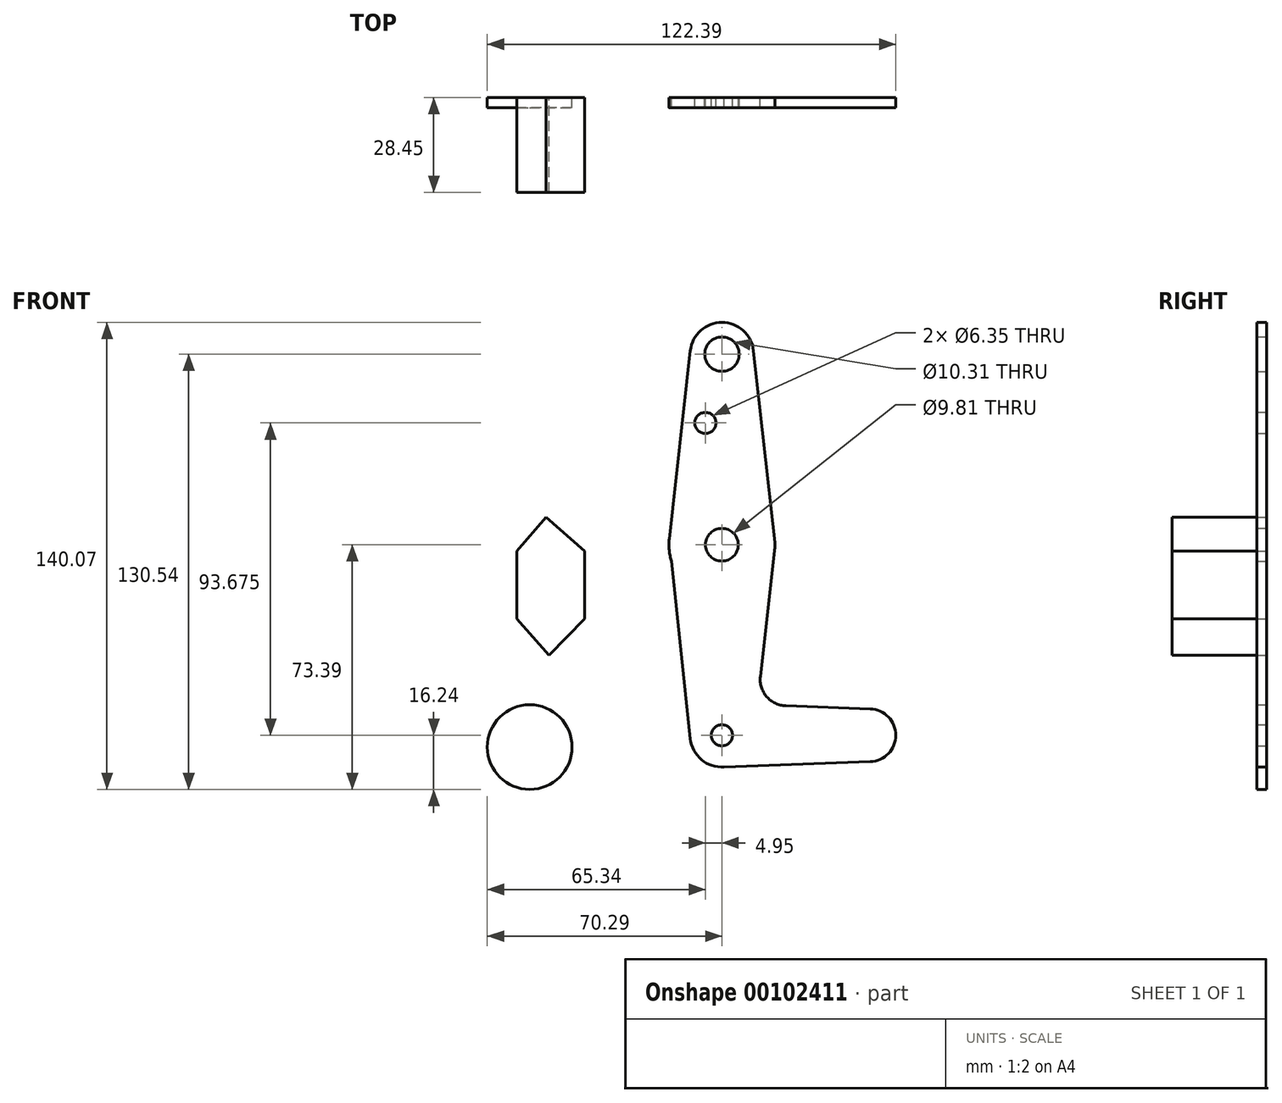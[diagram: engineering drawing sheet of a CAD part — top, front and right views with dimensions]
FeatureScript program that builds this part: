
annotation { "Feature Type Name" : "Feature", "Feature Type Description" : "" }
export const myFeature = defineFeature(function(context is Context, id is Id, definition is map)
    precondition{}
    {
        {
            var Q0;
            Q0=qCreatedBy(makeId("Front.planeOp"),FACE);
            var sketch = newSketch(context, id + "F0", { "sketchPlane" : qUnion([Q0])});
            skLineSegment(sketch, "E0", {"start": v(0, 114.3) * mm, "end": v(0, 0) * mm});
            skCircle(sketch, "E1", {"center": v(0, 114.3) * mm, "radius": 9.53 * mm});
            skCircle(sketch, "E2", {"center": v(0, 0) * mm, "radius": 9.53 * mm});
            skCircle(sketch, "E3", {"center": v(0, 57.15) * mm, "radius": 15.88 * mm});
            skCircle(sketch, "E4", {"center": v(0, 0) * mm, "radius": 3.18 * mm});
            skLineSegment(sketch, "E5", {"start": v(-9.47, 115.36) * mm, "end": v(-15.78, 58.91) * mm});
            skLineSegment(sketch, "E6", {"start": v(9.47, 115.36) * mm, "end": v(15.78, 58.91) * mm});
            skCircle(sketch, "E7", {"center": v(0, 57.15) * mm, "radius": 4.9 * mm});
            skLineSegment(sketch, "E8", {"start": v(-15.78, 58.91) * mm, "end": v(-9.47, -1) * mm});
            skLineSegment(sketch, "E9", {"start": v(11.52, 17.68) * mm, "end": v(15.77, 55.37) * mm});
            skCircle(sketch, "E10", {"center": v(-4.95, 93.68) * mm, "radius": 3.18 * mm});
            skCircle(sketch, "E11", {"center": v(44.17, 0) * mm, "radius": 7.94 * mm});
            skCircle(sketch, "E12", {"center": v(0, 114.3) * mm, "radius": 5.15 * mm});
            skLineSegment(sketch, "E13", {"start": v(19.14, 8.84) * mm, "end": v(44.45, 7.93) * mm});
            skLineSegment(sketch, "E14", {"start": v(0, -9.53) * mm, "end": v(44.45, -7.93) * mm});
            skPoint(sketch, "E15.newPointA", {"position": v(9.52, 0) * mm});
            skPoint(sketch, "E15.newPointB", {"position": v(0, 9.53) * mm});
            skArc(sketch, "E15.filletArc", {"start": v(11.52, 17.68) * mm, "mid": v(13.4, 11.6) * mm, "end": v(19.14, 8.84) * mm});
            skLineSegment(sketch, "E16.bottom", {"start": v(-61.44, 55.27) * mm, "end": v(-41.12, 55.27) * mm});
            skLineSegment(sketch, "E16.top", {"start": v(-61.44, 34.95) * mm, "end": v(-41.12, 34.95) * mm});
            skLineSegment(sketch, "E16.left", {"start": v(-61.44, 55.27) * mm, "end": v(-61.44, 34.95) * mm});
            skLineSegment(sketch, "E16.right", {"start": v(-41.12, 55.27) * mm, "end": v(-41.12, 34.95) * mm});
            skLineSegment(sketch, "E17", {"start": v(-61.44, 34.95) * mm, "end": v(-51.82, 23.95) * mm});
            skLineSegment(sketch, "E18", {"start": v(-51.82, 23.95) * mm, "end": v(-41.12, 34.95) * mm});
            skLineSegment(sketch, "E19", {"start": v(-61.44, 55.27) * mm, "end": v(-52.64, 65.46) * mm});
            skLineSegment(sketch, "E20", {"start": v(-52.64, 65.46) * mm, "end": v(-41.12, 55.27) * mm});
            skCircle(sketch, "E21", {"center": v(-57.6, -3.54) * mm, "radius": 12.7 * mm});
            skSolve(sketch);
        }
        {
            var Q0;
            Q0 = qSketchRegion(id + "F0", true);
            extrude(context, id + "F1", {"entities" : qUnion([Q0]), "depth" : 3.05 * mm});
        }
        {
            var Q0;
            Q0=makeQuery(id+"F1.opExtrude","CAP_FACE",FACE,{"disambiguationData":[OSD([sQuery(id+"F0.wireOp",EDGE,"E16.bottom"),sQuery(id+"F0.wireOp",EDGE,"E16.top"),sQuery(id+"F0.wireOp",EDGE,"E16.left"),sQuery(id+"F0.wireOp",EDGE,"E16.right")])],"isStart":false});
            extrude(context, id + "F2", {"entities" : qUnion([Q0]), "operationType" : NewBodyOperationType.ADD, "depth" : 25.4 * mm, "offsetDistance" : 25.4 * mm});
        }
    });
